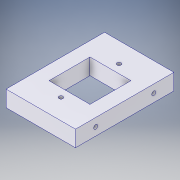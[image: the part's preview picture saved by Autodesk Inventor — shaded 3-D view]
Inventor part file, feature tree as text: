
AUTODESK INVENTOR PART (.ipt)
format: ipt  version: 2017 (Build 210142000, 142)  size: 138,240 bytes
history: native  units: in
note: dims shown in document units (in); Inventor stores cm internally (conversion verified against a paired STEP export)
features: extrude x5, sketch x5, projected_geometry x2
ambient origin geometry x8: Origin, YZ Plane, XZ Plane, XY Plane, X Axis, Y Axis, Z Axis, Center Point
bodies: Solid1 (feature_tree)
feature tree (12):
  extrude  "Extrusion1"  Depth=1.6929in
  extrude  "Extrusion2"  Depth=0.3937in
  extrude  "Extrusion3"  Depth=0.3937in TaperAngle=0.0deg
  extrude  "Extrusion4"  Depth=0.3937in
  extrude  "Extrusion5"  Depth=0.3937in
  sketch  "Sketch1"  dims[d0=2.4016in d1=1.6929in]
  sketch  "Sketch2"  dims[d2=0.3937in d3=0.0in d4=0.4921in]
  sketch  "Sketch3"  dims[d5=0.0984in d6=0.3937in d7=0.0in]
  projected_geometry  "Projected Loop1"
  sketch  "Sketch4"  dims[d8=0.3937in d9=0.0in d10=0.4921in]
  sketch  "Sketch5"  dims[d11=0.4921in d12=0.0984in d13=0.0984in d14=0.3937in d15=0.0in d16=1.0in d17=1.0in d18=0.3937in d19=0.0in]
  projected_geometry  "Projected Loop2"
